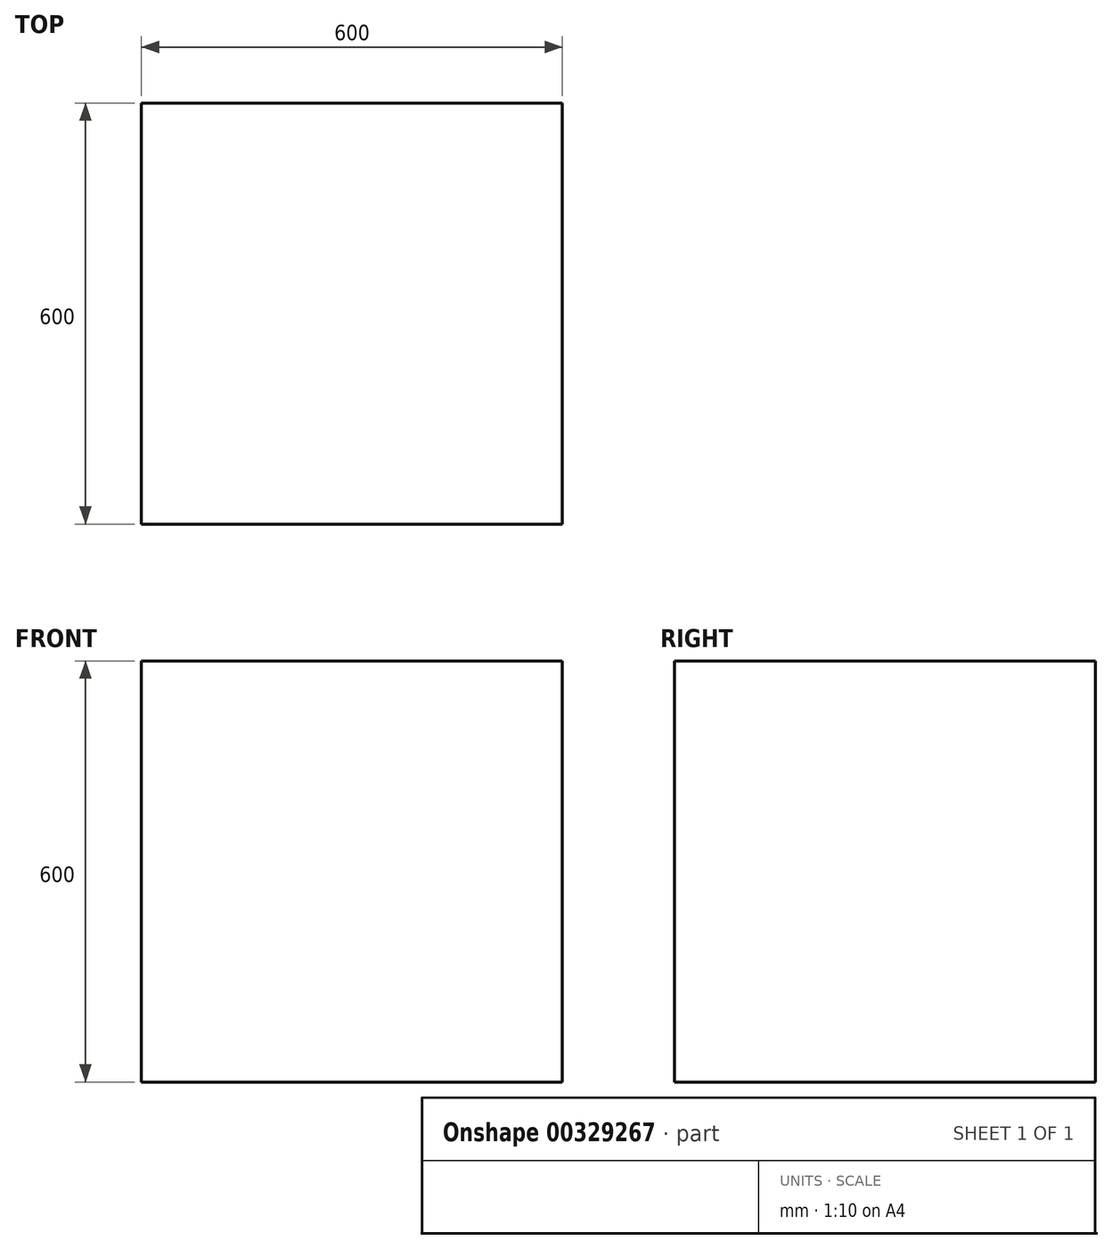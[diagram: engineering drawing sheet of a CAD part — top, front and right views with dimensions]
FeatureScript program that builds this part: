
annotation { "Feature Type Name" : "Feature", "Feature Type Description" : "" }
export const myFeature = defineFeature(function(context is Context, id is Id, definition is map)
    precondition{}
    {
        {
            var Q0;
            Q0=qCreatedBy(makeId("Front.planeOp"),FACE);
            var sketch = newSketch(context, id + "F0", { "sketchPlane" : qUnion([Q0])});
            skLineSegment(sketch, "E0.bottom", {"start": v(0, 0) * mm, "end": v(600, 0) * mm});
            skLineSegment(sketch, "E0.top", {"start": v(0, -600) * mm, "end": v(600, -600) * mm});
            skLineSegment(sketch, "E0.left", {"start": v(0, 0) * mm, "end": v(0, -600) * mm});
            skLineSegment(sketch, "E0.right", {"start": v(600, 0) * mm, "end": v(600, -600) * mm});
            skSolve(sketch);
        }
        {
            var Q0;
            Q0=makeQuery(id+"F0.imprint","IMPRINT",FACE,{"disambiguationData":[TD([[makeQuery(id+"F0.imprint","IMPRINT",EDGE,{"derivedFrom":sQuery(id+"F0.wireOp",EDGE,"E0.bottom")}),-1.0]])]});
            extrude(context, id + "F1", {"entities" : qUnion([Q0]), "depth" : 600 * mm});
        }
    });
